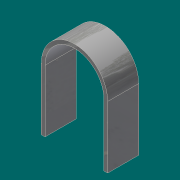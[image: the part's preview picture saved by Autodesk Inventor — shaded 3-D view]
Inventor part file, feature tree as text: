
AUTODESK INVENTOR PART (.ipt)
format: ipt  version: 2017 (Build 210142000, 142)  size: 117,248 bytes
history: native  units: in
note: dims shown in document units (in); Inventor stores cm internally (conversion verified against a paired STEP export)
features: extrude x1, sketch x1, other x1
ambient origin geometry x8: Origin, YZ Plane, XZ Plane, XY Plane, X Axis, Y Axis, Z Axis, Center Point
bodies: Solid1 (feature_tree)
feature tree (3):
  extrude  "Extrusion1"  Depth=0.12in
  sketch  "Sketch1"  dims[d0=1.9in d1=0.12in d2=2.0in d3=1.0in d4=0.0in]
  other  "Definition1"
